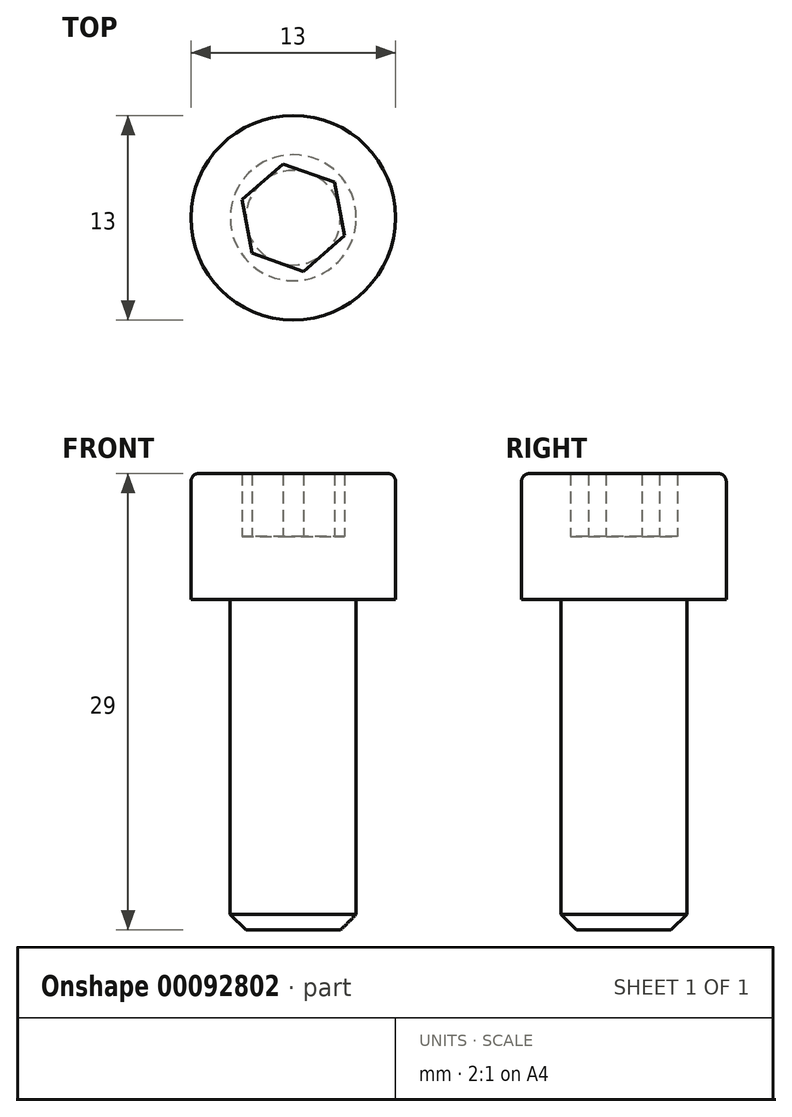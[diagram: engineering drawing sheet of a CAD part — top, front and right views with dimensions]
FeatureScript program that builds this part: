
annotation { "Feature Type Name" : "Feature", "Feature Type Description" : "" }
export const myFeature = defineFeature(function(context is Context, id is Id, definition is map)
    precondition{}
    {
        {
            var Q0;
            Q0=qCreatedBy(makeId("Top.planeOp"),FACE);
            var sketch = newSketch(context, id + "F0", { "sketchPlane" : qUnion([Q0])});
            skCircle(sketch, "E0", {"center": v(0, 0) * mm, "radius": 4 * mm});
            skCircle(sketch, "E1.cCircle", {"center": v(0, 0) * mm, "radius": 3 * mm, "construction": true});
            skLineSegment(sketch, "E1.0", {"start": v(-3.27, 1.15) * mm, "end": v(-0.64, 3.4) * mm});
            skLineSegment(sketch, "E1.1", {"start": v(-0.64, 3.4) * mm, "end": v(2.63, 2.26) * mm});
            skLineSegment(sketch, "E1.2", {"start": v(2.63, 2.26) * mm, "end": v(3.27, -1.15) * mm});
            skLineSegment(sketch, "E1.3", {"start": v(3.27, -1.15) * mm, "end": v(0.64, -3.4) * mm});
            skLineSegment(sketch, "E1.4", {"start": v(0.64, -3.4) * mm, "end": v(-2.63, -2.26) * mm});
            skLineSegment(sketch, "E1.5", {"start": v(-2.63, -2.26) * mm, "end": v(-3.27, 1.15) * mm});
            skPoint(sketch, "E1.0.midPoint", {"position": v(-1.96, 2.28) * mm});
            skCircle(sketch, "E2", {"center": v(0, 0) * mm, "radius": 6.5 * mm});
            skSolve(sketch);
        }
        {
            var Q0;
            Q0=qSketchRegion(id+"F0",true);
            var Q1;
            Q1=makeQuery(id+"F0.imprint","IMPRINT",FACE,{"disambiguationData":[TD([[makeQuery(id+"F0.imprint","IMPRINT",EDGE,{"derivedFrom":sQuery(id+"F0.wireOp",EDGE,"E0")}),1.0]])]});
            var Q2;
            Q2=makeQuery(id+"F0.imprint","IMPRINT",FACE,{"disambiguationData":[TD([[makeQuery(id+"F0.imprint","IMPRINT",EDGE,{"derivedFrom":sQuery(id+"F0.wireOp",EDGE,"E1.0")}),-1.0]])]});
            extrude(context, id + "F1", {"entities" : qUnion([Q0, Q1, Q2]), "oppositeDirection" : true, "depth" : 4 * mm});
        }
        {
            var Q0;
            Q0=makeQuery(id+"F0.imprint","IMPRINT",FACE,{"disambiguationData":[TD([[makeQuery(id+"F0.imprint","IMPRINT",EDGE,{"derivedFrom":sQuery(id+"F0.wireOp",EDGE,"E0")}),1.0]])]});
            var Q1;
            Q1=makeQuery(id+"F0.imprint","IMPRINT",FACE,{"disambiguationData":[TD([[makeQuery(id+"F0.imprint","IMPRINT",EDGE,{"derivedFrom":sQuery(id+"F0.wireOp",EDGE,"E0")}),-1.0]])]});
            extrude(context, id + "F2", {"entities" : qUnion([Q0, Q1]), "operationType" : NewBodyOperationType.ADD, "depth" : 4 * mm});
        }
        {
            var Q0;
            Q0=makeQuery(id+"F0.imprint","IMPRINT",FACE,{"disambiguationData":[TD([[makeQuery(id+"F0.imprint","IMPRINT",EDGE,{"derivedFrom":sQuery(id+"F0.wireOp",EDGE,"E1.0")}),-1.0]])]});
            var Q1;
            Q1=makeQuery(id+"F0.imprint","IMPRINT",FACE,{"disambiguationData":[TD([[makeQuery(id+"F0.imprint","IMPRINT",EDGE,{"derivedFrom":sQuery(id+"F0.wireOp",EDGE,"E0")}),1.0]])]});
            extrude(context, id + "F3", {"entities" : qUnion([Q0, Q1]), "operationType" : NewBodyOperationType.ADD, "oppositeDirection" : true, "depth" : 25 * mm});
        }
        {
            var Q0;
            Q0=makeQuery(id+"F2.opExtrude","CAP_EDGE",EDGE,{"disambiguationData":[OSD([sQuery(id+"F0.wireOp",EDGE,"E2")])],"isStart":false});
            fillet(context, id + "F4", {"entities" : qUnion([Q0]), "radius" : 0.5 * mm, "tangentPropagation" : true, "allowEdgeOverflow" : false});
        }
        {
            var Q0;
            Q0=makeQuery(id+"F3.opExtrude","CAP_FACE",FACE,{"disambiguationData":[OSD([sQuery(id+"F0.wireOp",EDGE,"E0")])],"isStart":false});
            chamfer(context, id + "F5", {"entities" : qUnion([Q0]), "width" : 1 * mm, "tangentPropagation" : true});
        }
    });
